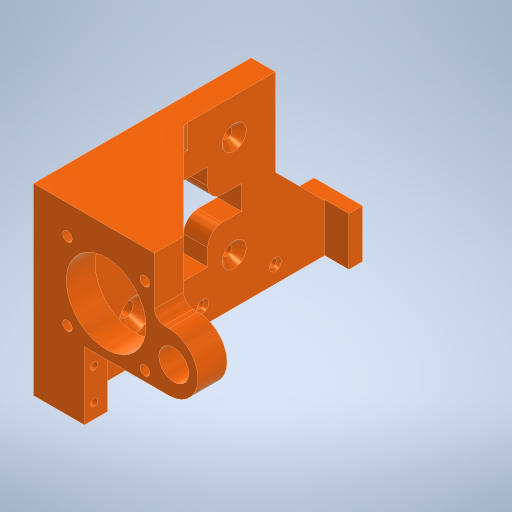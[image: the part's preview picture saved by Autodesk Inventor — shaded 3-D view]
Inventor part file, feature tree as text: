
AUTODESK INVENTOR PART (.ipt)
format: ipt  version: 2024.1 (Build 281209000, 209)  size: 475,136 bytes
history: native  units: in
note: dims shown in document units (in); Inventor stores cm internally (conversion verified against a paired STEP export)
features: extrude x18, sketch x18, chamfer x5, fillet x4
ambient origin geometry x8: Origin, YZ Plane, XZ Plane, XY Plane, X Axis, Y Axis, Z Axis, Center Point
bodies: Solid1 (feature_tree)
feature tree (45):
  extrude  "Extrusion1"  Depth=1.4961in
  extrude  "Extrusion2"  Depth=0.9449in
  extrude  "Extrusion3"  Depth=0.7874in TaperAngle=0.0deg
  extrude  "Extrusion4"  Depth=0.3937in
  extrude  "Extrusion5"  Depth=0.0787in
  fillet  "Fillet1"  Radius=0.0787in
  extrude  "Extrusion6"  Depth=0.0787in
  extrude  "Extrusion7"  Depth=0.315in
  chamfer  "Chamfer1"  [1 undecoded]
  chamfer  "Chamfer2"  Distance=0.7874in
  extrude  "Extrusion8"  Depth=0.0787in
  chamfer  "Chamfer3"  [1 undecoded]
  extrude  "Extrusion9"  Depth=0.1181in
  chamfer  "Chamfer4"  Distance=0.1181in
  extrude  "Extrusion10"  Depth=0.1575in
  extrude  "Extrusion15"  Depth=0.0787in
  extrude  "Extrusion16"  Depth=0.0787in
  extrude  "Extrusion17"  Depth=0.1575in
  extrude  "Extrusion18"  TaperAngle=0.0deg  [1 undecoded]
  extrude  "Extrusion19"  Depth=0.0591in TaperAngle=45.0deg
  chamfer  "Chamfer5"  Distance=0.0787in Angle=45.0deg
  extrude  "Extrusion20"  Depth=1.1024in
  extrude  "Extrusion21"  Depth=0.3937in
  fillet  "Fillet3"  [1 undecoded]
  extrude  "Extrusion22"  Depth=0.3937in TaperAngle=45.0deg
  fillet  "Fillet5"  Radius=0.0787in
  fillet  "Fillet6"  Radius=0.0787in
  sketch  "Sketch1"  dims[d0=1.4961in d1=2.1654in]
  sketch  "Sketch2"  dims[d2=0.1969in d3=0.0in d4=0.9449in]
  sketch  "Sketch3"  dims[d5=0.2362in d6=0.7874in d7=0.0in]
  sketch  "Sketch4"  dims[d8=0.6496in d9=0.3937in]
  sketch  "Sketch5"  dims[d10=0.3937in d11=0.0787in d12=0.0787in]
  sketch  "Sketch6"  dims[d13=0.0787in d14=0.0787in]
  sketch  "Sketch7"  dims[d15=0.315in d16=0.315in]
  sketch  "Sketch8"  dims[d17=0.315in]
  sketch  "Sketch9"  dims[d18=0.315in]
  sketch  "Sketch10"  dims[d19=0.315in]
  sketch  "Sketch15"  dims[d20=0.315in]
  sketch  "Sketch16"  dims[d21=0.315in]
  sketch  "Sketch17"  dims[d22=0.315in d23=0.0in d24=0.0in]
  sketch  "Sketch18"  dims[d25=0.1181in d26=0.7874in d27=0.0in]
  sketch  "Sketch19"  dims[d28=0.0in d29=0.0in d30=0.0787in]
  sketch  "Sketch20"  dims[d31=0.0787in]
  sketch  "Sketch21"  dims[d32=0.7087in]
  sketch  "Sketch22"  dims[d33=1.378in d34=0.0in d35=0.0in d36=0.1181in d37=0.1181in d38=0.1575in d39=0.4331in d40=0.4331in d41=0.1575in d42=0.0in d43=0.0in d44=0.0591in d45=0.0787in d46=45.0deg d47=0.0748in d48=0.0787in d49=45.0deg d50=1.1024in d51=0.3937in d52=0.0in d53=0.0in d54=0.3937in d55=0.0787in d56=45.0deg d57=0.0787in d58=0.0787in d59=0.2953in d60=0.7283in d61=0.374in d62=0.7283in d63=0.0in d64=0.0in d65=0.0591in d66=0.0787in d67=45.0deg d68=0.0591in d69=0.0591in d70=0.0591in d71=0.1378in d72=0.3937in d73=0.1378in d74=0.5906in d76=0.1378in d77=0.0in d78=0.0in d95=0.5906in d96=0.1181in d97=0.3937in d98=0.2165in d99=0.0in d100=0.1102in d101=0.1969in d102=0.0in d103=0.189in d104=0.2165in d105=0.0in d106=0.0591in d107=0.0591in d108=0.2559in d109=0.1181in d110=0.0787in d111=0.0787in d112=0.0in d113=0.0in d114=0.1969in d115=0.3937in d116=0.3937in d117=0.5512in d118=0.0in d119=0.0in d120=0.0197in d121=0.0787in d122=45.0deg d123=0.4724in d124=0.3543in d125=0.0in d126=0.2441in d127=0.2362in d128=0.1969in d129=0.0in d130=0.0in d132=0.2362in d134=0.1969in d135=0.2559in d136=0.2756in d137=0.0in d138=0.0in d139=0.1181in d152=0.0787in]
note: 4 required parameter values undecoded (feature->parameter linkage not recoverable at this tier; creation-order binding heuristic only, values carry confidence <= 0.55)
